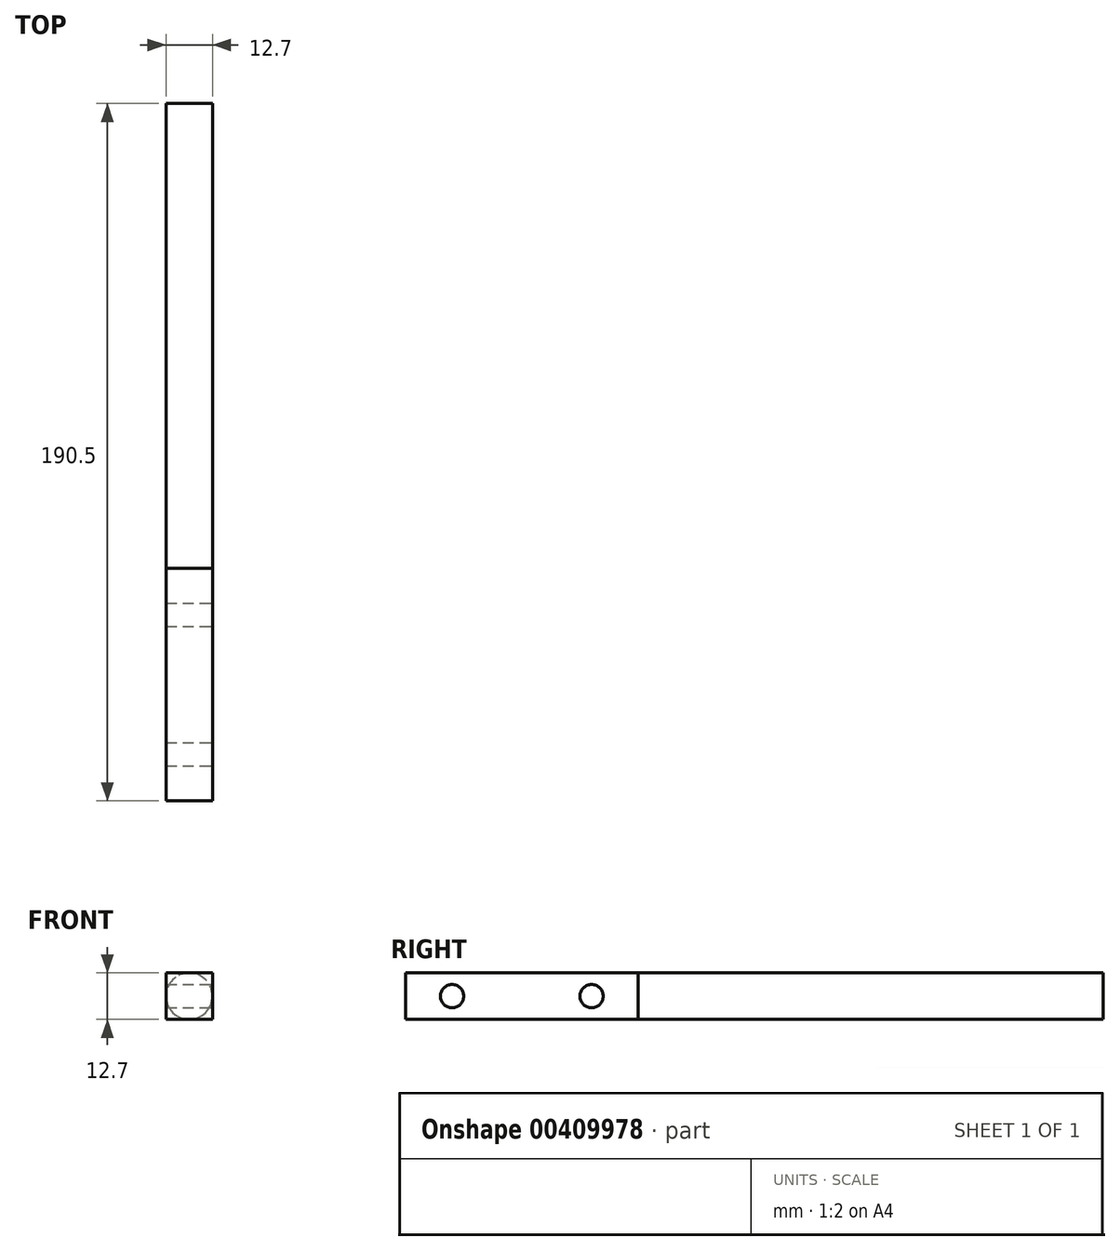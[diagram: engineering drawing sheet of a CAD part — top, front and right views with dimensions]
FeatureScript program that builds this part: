
annotation { "Feature Type Name" : "Feature", "Feature Type Description" : "" }
export const myFeature = defineFeature(function(context is Context, id is Id, definition is map)
    precondition{}
    {
        {
            var Q0;
            Q0=qCreatedBy(makeId("Front.planeOp"),FACE);
            var sketch = newSketch(context, id + "F0", { "sketchPlane" : qUnion([Q0])});
            skLineSegment(sketch, "E0.bottom", {"start": v(-6.35, 6.35) * mm, "end": v(6.35, 6.35) * mm});
            skLineSegment(sketch, "E0.top", {"start": v(-6.35, -6.35) * mm, "end": v(6.35, -6.35) * mm});
            skLineSegment(sketch, "E0.left", {"start": v(-6.35, 6.35) * mm, "end": v(-6.35, -6.35) * mm});
            skLineSegment(sketch, "E0.right", {"start": v(6.35, 6.35) * mm, "end": v(6.35, -6.35) * mm});
            skSolve(sketch);
        }
        {
            var Q0;
            Q0 = qSketchRegion(id + "F0", true);
            extrude(context, id + "F1", {"entities" : qUnion([Q0]), "depth" : 63.5 * mm});
        }
        {
            var Q0;
            Q0=makeQuery(id+"F1.opExtrude","CAP_FACE",FACE,{"disambiguationData":[OSD([sQuery(id+"F0.wireOp",EDGE,"E0.bottom"),sQuery(id+"F0.wireOp",EDGE,"E0.top"),sQuery(id+"F0.wireOp",EDGE,"E0.left"),sQuery(id+"F0.wireOp",EDGE,"E0.right")])],"isStart":true});
            var sketch = newSketch(context, id + "F2", { "sketchPlane" : qUnion([Q0])});
            skCircle(sketch, "E1", {"center": v(0, 0) * mm, "radius": 6.35 * mm});
            skSolve(sketch);
        }
        {
            var Q0;
            Q0 = qSketchRegion(id + "F2", true);
            extrude(context, id + "F3", {"entities" : qUnion([Q0]), "operationType" : NewBodyOperationType.ADD, "depth" : 127 * mm});
        }
        {
            var Q0;
            Q0=makeQuery(id+"F1.opExtrude","SWEPT_FACE",FACE,{"disambiguationData":[OSD([sQuery(id+"F0.wireOp",EDGE,"E0.right")])]});
            var sketch = newSketch(context, id + "F4", { "sketchPlane" : qUnion([Q0])});
            skPoint(sketch, "E2", {"position": v(-12.7, 0) * mm});
            skPoint(sketch, "E3", {"position": v(-50.8, 0) * mm});
            skSolve(sketch);
        }
        {
            var Q0;
            Q0=sQuery(id+"F4.wireOp",VERTEX,"E2");
            var Q1;
            Q1=sQuery(id+"F4.wireOp",VERTEX,"E3");
            var Q2;
            Q2=makeQuery(id+"F1.opExtrude","SWEPT_BODY",BODY,{"disambiguationData":[OSD([sQuery(id+"F0.wireOp",EDGE,"E0.bottom"),sQuery(id+"F0.wireOp",EDGE,"E0.top"),sQuery(id+"F0.wireOp",EDGE,"E0.left"),sQuery(id+"F0.wireOp",EDGE,"E0.right")])]});
            hole(context, id + "F5", {"style" : HoleStyle.SIMPLE, "endStyle" : HoleEndStyle.THROUGH, "holeDiameter" : 6.35 * mm, "isTappedThrough" : true, "tappedDepth" : 12.7 * mm, "tapClearance" : 3, "locations" : qUnion([Q0, Q1]), "scope" : qUnion([Q2])});
        }
    });
